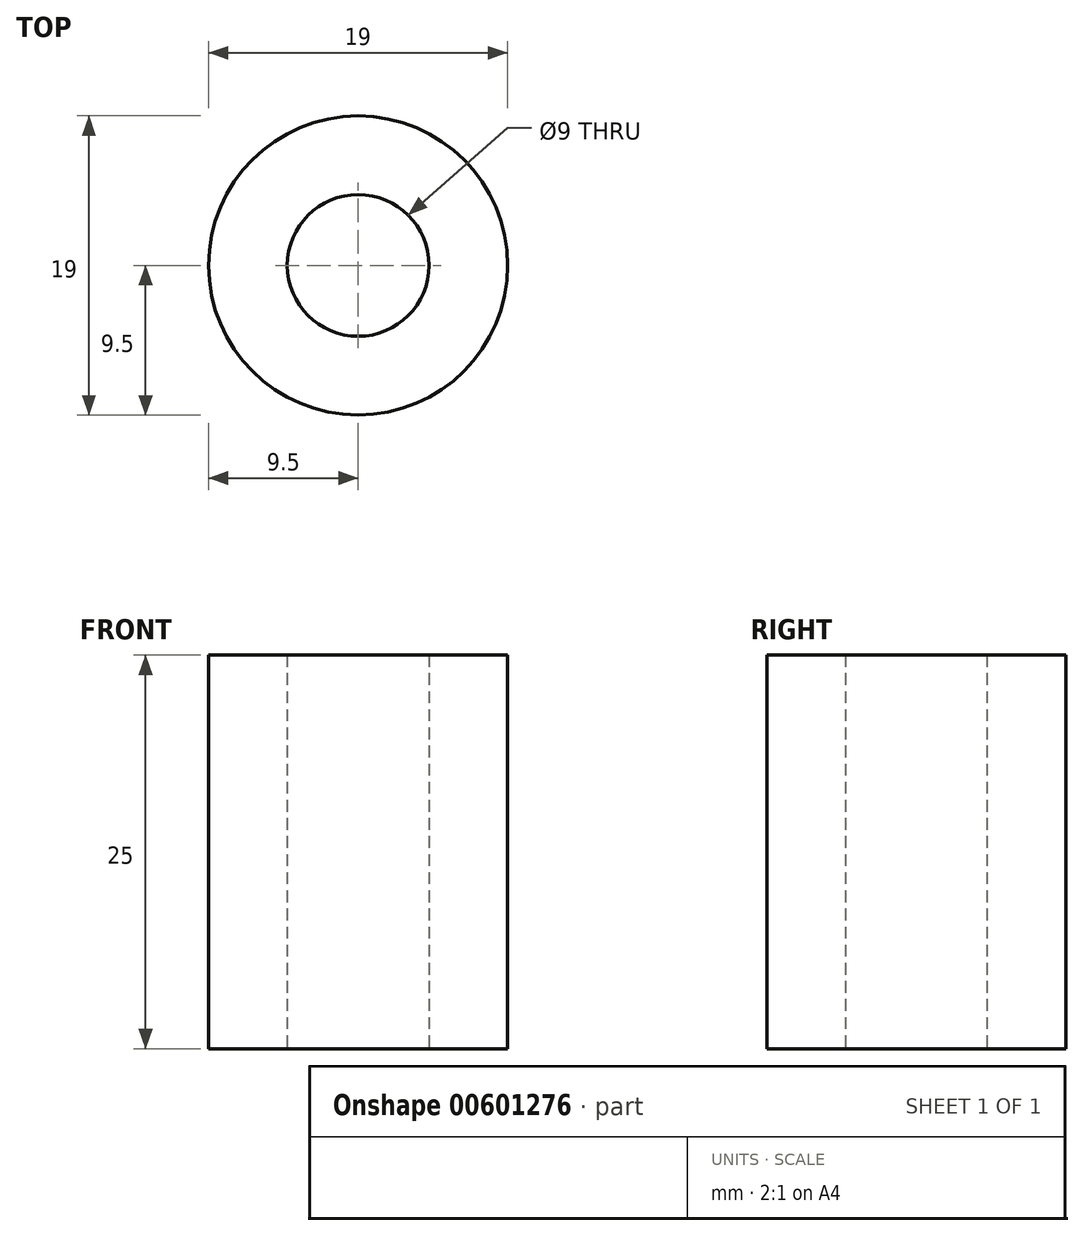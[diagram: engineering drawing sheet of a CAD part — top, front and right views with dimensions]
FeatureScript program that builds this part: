
annotation { "Feature Type Name" : "Feature", "Feature Type Description" : "" }
export const myFeature = defineFeature(function(context is Context, id is Id, definition is map)
    precondition{}
    {
        {
            var Q0;
            Q0=qCreatedBy(makeId("Top.planeOp"),FACE);
            var sketch = newSketch(context, id + "F0", { "sketchPlane" : qUnion([Q0])});
            skCircle(sketch, "E0", {"center": v(0, 0) * mm, "radius": 9.5 * mm});
            skCircle(sketch, "E1", {"center": v(0, 0) * mm, "radius": 4.5 * mm});
            skPoint(sketch, "E2", {"position": v(0, -9.5) * mm});
            skSolve(sketch);
        }
        {
            var Q0;
            Q0 = qSketchRegion(id + "F0", true);
            extrude(context, id + "F1", {"entities" : qUnion([Q0]), "endBound" : BoundingType.SYMMETRIC, "depth" : 25 * mm, "offsetDistance" : 25.4 * mm});
        }
        {
            var Q0;
            Q0=sQuery(id+"F0.wireOp",VERTEX,"E2");
            var Q1;
            Q1=qCreatedBy(makeId("Front.planeOp"),FACE);
            cPlane(context, id + "F2", {"entities" : qUnion([Q0, Q1]), "cplaneType" : CPlaneType.PLANE_POINT, "offset" : 25 * mm, "width" : 150 * mm, "height" : 150 * mm});
        }
    });
